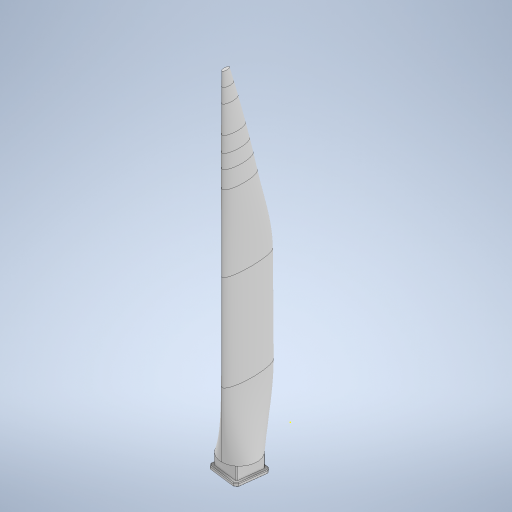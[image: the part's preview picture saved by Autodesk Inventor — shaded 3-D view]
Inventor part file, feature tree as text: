
AUTODESK INVENTOR PART (.ipt)
format: ipt  version: 2023 (Build 270158000, 158)  size: 556,544 bytes
history: native  units: in
note: dims shown in document units (in); Inventor stores cm internally (conversion verified against a paired STEP export)
features: sketch x5, extrude x4, chamfer x3, other x1
ambient origin geometry x8: Origin, YZ Plane, XZ Plane, XY Plane, X Axis, Y Axis, Z Axis, Center Point
bodies: Solid1 (feature_tree)
feature tree (13):
  extrude  "Extrusion1"  Depth=0.7283in
  sketch  "Sketch6"  dims[d15=0.6665in d16=0.7283in]
  sketch  "Sketch7"  dims[d17=0.1969in d18=0.1969in]
  extrude  "Extrusion4"  Depth=0.7283in
  extrude  "Extrusion5"  Depth=0.1969in
  extrude  "Extrusion6"  Depth=0.3937in
  chamfer  "Chamfer2"  [1 undecoded]
  chamfer  "Chamfer3"  Distance=0.7283in
  chamfer  "Chamfer4"  Distance=0.5703in
  sketch  "Sketch1"  dims[d0=0.4724in d1=0.0in d14=0.7283in]
  sketch  "Sketch8"  dims[d19=0.3937in d20=0.0in d21=0.9843in]
  sketch  "Sketch11"  dims[d22=0.4921in d23=0.0in d24=0.7283in d25=0.5703in d26=0.7283in d27=0.3504in d28=0.0in d30=0.3642in d33=0.3642in d34=0.8858in d35=0.8858in d36=0.3642in d37=0.3642in d38=0.0984in d39=0.0in d43=0.0787in d44=0.0787in d45=45.0deg d46=0.0197in d47=0.0787in d48=45.0deg d49=0.0197in d50=0.0787in d51=45.0deg]
  other  "Trennlinie1"
note: 1 required parameter value undecoded (feature->parameter linkage not recoverable at this tier; creation-order binding heuristic only, values carry confidence <= 0.55)
